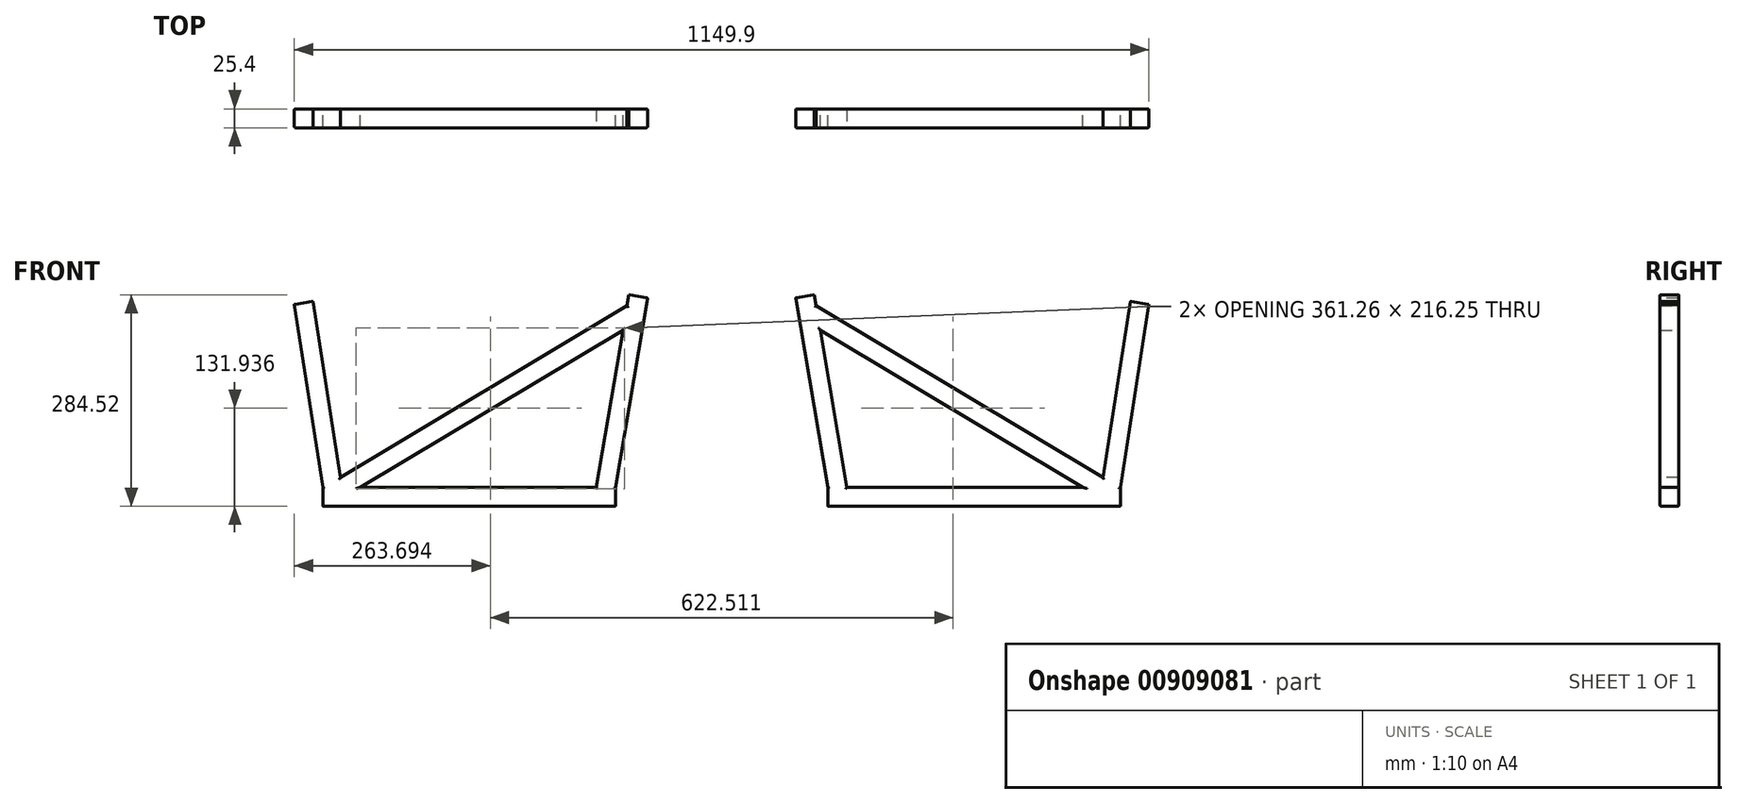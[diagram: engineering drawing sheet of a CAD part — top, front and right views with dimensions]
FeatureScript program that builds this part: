
annotation { "Feature Type Name" : "Feature", "Feature Type Description" : "" }
export const myFeature = defineFeature(function(context is Context, id is Id, definition is map)
    precondition{}
    {
        {
            var Q0;
            Q0=qCreatedBy(makeId("Front.planeOp"),FACE);
            var sketch = newSketch(context, id + "F0", { "sketchPlane" : qUnion([Q0])});
            skLineSegment(sketch, "E0", {"start": v(0, 0) * mm, "end": v(0, -387.35) * mm, "construction": true});
            skLineSegment(sketch, "E1", {"start": v(0, -387.35) * mm, "end": v(-552.45, -387.35) * mm, "construction": true});
            skLineSegment(sketch, "E2", {"start": v(-552.45, -387.35) * mm, "end": v(-574.68, -387.35) * mm, "construction": true});
            skCircle(sketch, "E3", {"center": v(-574.68, -387.35) * mm, "radius": 22.23 * mm});
            skLineSegment(sketch, "E4", {"start": v(0, -387.35) * mm, "end": v(0, -679.45) * mm, "construction": true});
            skLineSegment(sketch, "E5", {"start": v(0, -679.45) * mm, "end": v(-536.58, -679.45) * mm, "construction": true});
            skLineSegment(sketch, "E6", {"start": v(-536.58, -654.05) * mm, "end": v(-142.87, -654.05) * mm});
            skLineSegment(sketch, "E7", {"start": v(-574.68, -387.35) * mm, "end": v(-574.68, -409.58) * mm});
            skLineSegment(sketch, "E8", {"start": v(-574.68, -409.58) * mm, "end": v(0, -409.58) * mm, "construction": true});
            skLineSegment(sketch, "E9", {"start": v(0, -409.58) * mm, "end": v(-114.3, -409.58) * mm, "construction": true});
            skCircle(sketch, "E10", {"center": v(-114.3, -409.58) * mm, "radius": 12.7 * mm});
            skLineSegment(sketch, "E11", {"start": v(-536.58, -654.05) * mm, "end": v(-536.58, -679.45) * mm});
            skLineSegment(sketch, "E12", {"start": v(-536.58, -679.45) * mm, "end": v(-142.87, -679.45) * mm});
            skLineSegment(sketch, "E13", {"start": v(-142.87, -679.45) * mm, "end": v(-142.87, -654.05) * mm});
            skLineSegment(sketch, "E14", {"start": v(-536.58, -666.75) * mm, "end": v(-142.87, -666.75) * mm});
            skLineSegment(sketch, "E15", {"start": v(-574.68, -409.58) * mm, "end": v(-536.58, -654.05) * mm});
            skLineSegment(sketch, "E16", {"start": v(-555.63, -531.81) * mm, "end": v(-530.53, -527.9) * mm});
            skLineSegment(sketch, "E17", {"start": v(-530.53, -527.9) * mm, "end": v(-510.87, -654.05) * mm});
            skLineSegment(sketch, "E18", {"start": v(-530.53, -527.9) * mm, "end": v(-552.45, -387.23) * mm});
            skLineSegment(sketch, "E19", {"start": v(-142.87, -654.05) * mm, "end": v(-101.78, -411.7) * mm});
            skLineSegment(sketch, "E20", {"start": v(-101.78, -411.7) * mm, "end": v(-101.42, -409.58) * mm});
            skLineSegment(sketch, "E21", {"start": v(-122.33, -532.87) * mm, "end": v(-147.37, -528.63) * mm});
            skLineSegment(sketch, "E22", {"start": v(-147.37, -528.63) * mm, "end": v(-168.64, -654.05) * mm});
            skLineSegment(sketch, "E23", {"start": v(-147.37, -528.63) * mm, "end": v(-126.82, -407.45) * mm});
            skCircle(sketch, "E24", {"center": v(-510.87, -654.05) * mm, "radius": 12.7 * mm});
            skLineSegment(sketch, "E25", {"start": v(-127.18, -409.58) * mm, "end": v(-517.4, -643.15) * mm});
            skLineSegment(sketch, "E26", {"start": v(-322.29, -526.36) * mm, "end": v(-309.24, -548.16) * mm});
            skLineSegment(sketch, "E27", {"start": v(-309.24, -548.16) * mm, "end": v(-315.76, -537.26) * mm});
            skLineSegment(sketch, "E28", {"start": v(-309.24, -548.16) * mm, "end": v(-132.77, -442.52) * mm});
            skLineSegment(sketch, "E29", {"start": v(-309.24, -548.16) * mm, "end": v(-486.14, -654.05) * mm});
            skLineSegment(sketch, "E30", {"start": v(-339.72, -654.05) * mm, "end": v(-339.72, -679.45) * mm});
            skLineSegment(sketch, "E31", {"start": v(-315.76, -537.26) * mm, "end": v(-120.74, -420.52) * mm});
            skLineSegment(sketch, "E32", {"start": v(-315.76, -537.26) * mm, "end": v(-510.87, -654.05) * mm});
            skLineSegment(sketch, "E33", {"start": v(-543.08, -529.86) * mm, "end": v(-562.4, -405.88) * mm});
            skLineSegment(sketch, "E34", {"start": v(-543.08, -529.86) * mm, "end": v(-523.72, -654.05) * mm});
            skLineSegment(sketch, "E35", {"start": v(-134.85, -530.75) * mm, "end": v(-157.9, -666.75) * mm});
            skLineSegment(sketch, "E36", {"start": v(-523.72, -654.05) * mm, "end": v(-521.74, -666.75) * mm});
            skLineSegment(sketch, "E37", {"start": v(-134.85, -530.75) * mm, "end": v(-112.18, -397.05) * mm});
            skLineSegment(sketch, "E38", {"start": v(-510.87, -654.05) * mm, "end": v(-521.77, -660.57) * mm});
            skSolve(sketch);
        }
        {
            var Q0;
            Q0=sQuery(id+"F0.wireOp",EDGE,"E34");
            var Q1;
            Q1=sQuery(id+"F0.wireOp",VERTEX,"E33.start");
            cPlane(context, id + "F1", {"entities" : qUnion([Q0, Q1]), "cplaneType" : CPlaneType.LINE_POINT, "offset" : 25.4 * mm, "width" : 152.4 * mm, "height" : 152.4 * mm});
        }
        {
            var Q0;
            Q0=sQuery(id+"F0.wireOp",EDGE,"E26");
            cPoint(context, id + "F2", {"entities" : qUnion([Q0]), "parameter" : 0.5});
        }
        {
            var Q0;
            Q0=sQuery(id+"F0.wireOp",EDGE,"E32");
            var Q1;
            Q1 = qCreatedBy(id + "F2" ,VERTEX);
            cPlane(context, id + "F3", {"entities" : qUnion([Q0, Q1]), "cplaneType" : CPlaneType.LINE_POINT, "offset" : 25.4 * mm, "width" : 152.4 * mm, "height" : 152.4 * mm});
        }
        {
            var Q0;
            Q0=sQuery(id+"F0.wireOp",EDGE,"E35");
            var Q1;
            Q1=sQuery(id+"F0.wireOp",VERTEX,"E35.start");
            cPlane(context, id + "F4", {"entities" : qUnion([Q0, Q1]), "cplaneType" : CPlaneType.LINE_POINT, "offset" : 25.4 * mm, "width" : 152.4 * mm, "height" : 152.4 * mm});
        }
        {
            var Q0;
            Q0=sQuery(id+"F0.wireOp",EDGE,"E14");
            cPoint(context, id + "F5", {"entities" : qUnion([Q0]), "parameter" : 0.5});
        }
        {
            var Q0;
            Q0=sQuery(id+"F0.wireOp",EDGE,"E14");
            var Q1;
            Q1 = qCreatedBy(id + "F5" ,VERTEX);
            cPlane(context, id + "F6", {"entities" : qUnion([Q0, Q1]), "cplaneType" : CPlaneType.LINE_POINT, "offset" : 25.4 * mm, "width" : 152.4 * mm, "height" : 152.4 * mm});
        }
        {
            var Q0;
            Q0=qCreatedBy(id+"F1.planeOp",FACE);
            var sketch = newSketch(context, id + "F7", { "sketchPlane" : qUnion([Q0])});
            skLineSegment(sketch, "E39.bottom", {"start": v(-607.08, -12.7) * mm, "end": v(-629.3, -12.7) * mm});
            skLineSegment(sketch, "E39.top", {"start": v(-607.08, 12.7) * mm, "end": v(-629.3, 12.7) * mm});
            skLineSegment(sketch, "E39.left", {"start": v(-605.49, -11.11) * mm, "end": v(-605.49, 11.11) * mm});
            skLineSegment(sketch, "E39.right", {"start": v(-630.89, -11.11) * mm, "end": v(-630.89, 11.11) * mm});
            skPoint(sketch, "E39.middle", {"position": v(-618.19, 0) * mm});
            skPoint(sketch, "E40.visualSharp", {"position": v(-630.89, 12.7) * mm});
            skArc(sketch, "E40.filletArc", {"start": v(-629.3, 12.7) * mm, "mid": v(-630.42, 12.24) * mm, "end": v(-630.89, 11.11) * mm});
            skPoint(sketch, "E41.visualSharp", {"position": v(-605.49, 12.7) * mm});
            skArc(sketch, "E41.filletArc", {"start": v(-605.49, 11.11) * mm, "mid": v(-605.95, 12.24) * mm, "end": v(-607.08, 12.7) * mm});
            skPoint(sketch, "E42.visualSharp", {"position": v(-605.49, -12.7) * mm});
            skArc(sketch, "E42.filletArc", {"start": v(-607.08, -12.7) * mm, "mid": v(-605.95, -12.24) * mm, "end": v(-605.49, -11.11) * mm});
            skPoint(sketch, "E43.visualSharp", {"position": v(-630.89, -12.7) * mm});
            skArc(sketch, "E43.filletArc", {"start": v(-630.89, -11.11) * mm, "mid": v(-630.42, -12.24) * mm, "end": v(-629.3, -12.7) * mm});
            skSolve(sketch);
        }
        {
            var Q0;
            Q0=qCreatedBy(id+"F4.planeOp",FACE);
            var sketch = newSketch(context, id + "F8", { "sketchPlane" : qUnion([Q0])});
            skLineSegment(sketch, "E44.bottom", {"start": v(-33.1, -12.7) * mm, "end": v(-55.33, -12.7) * mm});
            skLineSegment(sketch, "E44.top", {"start": v(-33.1, 12.7) * mm, "end": v(-55.33, 12.7) * mm});
            skLineSegment(sketch, "E44.left", {"start": v(-31.52, -11.11) * mm, "end": v(-31.52, 11.11) * mm});
            skLineSegment(sketch, "E44.right", {"start": v(-56.92, -11.11) * mm, "end": v(-56.92, 11.11) * mm});
            skPoint(sketch, "E44.middle", {"position": v(-44.22, 0) * mm});
            skPoint(sketch, "E45.visualSharp", {"position": v(-56.92, 12.7) * mm});
            skArc(sketch, "E45.filletArc", {"start": v(-55.33, 12.7) * mm, "mid": v(-56.45, 12.24) * mm, "end": v(-56.92, 11.11) * mm});
            skPoint(sketch, "E46.visualSharp", {"position": v(-31.52, 12.7) * mm});
            skArc(sketch, "E46.filletArc", {"start": v(-31.52, 11.11) * mm, "mid": v(-31.98, 12.24) * mm, "end": v(-33.1, 12.7) * mm});
            skPoint(sketch, "E47.visualSharp", {"position": v(-31.52, -12.7) * mm});
            skArc(sketch, "E47.filletArc", {"start": v(-33.1, -12.7) * mm, "mid": v(-31.98, -12.24) * mm, "end": v(-31.52, -11.11) * mm});
            skPoint(sketch, "E48.visualSharp", {"position": v(-56.92, -12.7) * mm});
            skArc(sketch, "E48.filletArc", {"start": v(-56.92, -11.11) * mm, "mid": v(-56.45, -12.24) * mm, "end": v(-55.33, -12.7) * mm});
            skSolve(sketch);
        }
        {
            var Q0;
            Q0=qCreatedBy(id+"F3.planeOp",FACE);
            var sketch = newSketch(context, id + "F9", { "sketchPlane" : qUnion([Q0])});
            skLineSegment(sketch, "E49.bottom", {"start": v(-11.11, -311.5) * mm, "end": v(11.11, -311.5) * mm});
            skLineSegment(sketch, "E49.top", {"start": v(-11.11, -286.1) * mm, "end": v(11.11, -286.1) * mm});
            skLineSegment(sketch, "E49.left", {"start": v(-12.7, -309.92) * mm, "end": v(-12.7, -287.7) * mm});
            skLineSegment(sketch, "E49.right", {"start": v(12.7, -309.92) * mm, "end": v(12.7, -287.7) * mm});
            skPoint(sketch, "E49.middle", {"position": v(0, -298.8) * mm});
            skPoint(sketch, "E50.visualSharp", {"position": v(12.7, -286.1) * mm});
            skArc(sketch, "E50.filletArc", {"start": v(12.7, -287.7) * mm, "mid": v(12.24, -286.57) * mm, "end": v(11.11, -286.1) * mm});
            skPoint(sketch, "E51.visualSharp", {"position": v(12.7, -311.5) * mm});
            skArc(sketch, "E51.filletArc", {"start": v(11.11, -311.5) * mm, "mid": v(12.24, -311.04) * mm, "end": v(12.7, -309.92) * mm});
            skPoint(sketch, "E52.visualSharp", {"position": v(-12.7, -311.5) * mm});
            skArc(sketch, "E52.filletArc", {"start": v(-12.7, -309.92) * mm, "mid": v(-12.24, -311.04) * mm, "end": v(-11.11, -311.5) * mm});
            skPoint(sketch, "E53.visualSharp", {"position": v(-12.7, -286.1) * mm});
            skArc(sketch, "E53.filletArc", {"start": v(-11.11, -286.1) * mm, "mid": v(-12.24, -286.57) * mm, "end": v(-12.7, -287.7) * mm});
            skSolve(sketch);
        }
        {
            var Q0;
            Q0=qCreatedBy(id+"F6.planeOp",FACE);
            var sketch = newSketch(context, id + "F10", { "sketchPlane" : qUnion([Q0])});
            skLineSegment(sketch, "E54.bottom", {"start": v(-11.11, -679.45) * mm, "end": v(11.11, -679.45) * mm});
            skLineSegment(sketch, "E54.top", {"start": v(-11.11, -654.05) * mm, "end": v(11.11, -654.05) * mm});
            skLineSegment(sketch, "E54.left", {"start": v(-12.7, -677.86) * mm, "end": v(-12.7, -655.64) * mm});
            skLineSegment(sketch, "E54.right", {"start": v(12.7, -677.86) * mm, "end": v(12.7, -655.64) * mm});
            skPoint(sketch, "E54.middle", {"position": v(0, -666.75) * mm});
            skPoint(sketch, "E55.visualSharp", {"position": v(-12.7, -654.05) * mm});
            skArc(sketch, "E55.filletArc", {"start": v(-11.11, -654.05) * mm, "mid": v(-12.24, -654.51) * mm, "end": v(-12.7, -655.64) * mm});
            skPoint(sketch, "E56.visualSharp", {"position": v(-12.7, -679.45) * mm});
            skArc(sketch, "E56.filletArc", {"start": v(-12.7, -677.86) * mm, "mid": v(-12.24, -678.99) * mm, "end": v(-11.11, -679.45) * mm});
            skPoint(sketch, "E57.visualSharp", {"position": v(12.7, -679.45) * mm});
            skArc(sketch, "E57.filletArc", {"start": v(11.11, -679.45) * mm, "mid": v(12.24, -678.99) * mm, "end": v(12.7, -677.86) * mm});
            skPoint(sketch, "E58.visualSharp", {"position": v(12.7, -654.05) * mm});
            skArc(sketch, "E58.filletArc", {"start": v(12.7, -655.64) * mm, "mid": v(12.24, -654.51) * mm, "end": v(11.11, -654.05) * mm});
            skSolve(sketch);
        }
        {
            var Q0;
            Q0=makeQuery(id+"F7.imprint","IMPRINT",FACE,{"disambiguationData":[TD([[makeQuery(id+"F7.imprint","IMPRINT",EDGE,{"derivedFrom":sQuery(id+"F7.wireOp",EDGE,"E39.bottom")}),-1.0]])]});
            var Q1;
            Q1=sQuery(id+"F0.wireOp",EDGE,"E33");
            var Q2;
            Q2=sQuery(id+"F0.wireOp",EDGE,"E34");
            var Q3;
            Q3=sQuery(id+"F0.wireOp",EDGE,"E36");
            sweep(context, id + "F11", {"profiles" : qUnion([Q0]), "path" : qUnion([Q1, Q2, Q3])});
        }
        {
            var Q0;
            Q0=makeQuery(id+"F10.imprint","IMPRINT",FACE,{"disambiguationData":[TD([[makeQuery(id+"F10.imprint","IMPRINT",EDGE,{"derivedFrom":sQuery(id+"F10.wireOp",EDGE,"E54.bottom")}),1.0]])]});
            var Q1;
            Q1=sQuery(id+"F0.wireOp",EDGE,"E14");
            sweep(context, id + "F12", {"operationType" : NewBodyOperationType.ADD, "profiles" : qUnion([Q0]), "path" : qUnion([Q1])});
        }
        {
            var Q0;
            Q0=makeQuery(id+"F9.imprint","IMPRINT",FACE,{"disambiguationData":[TD([[makeQuery(id+"F9.imprint","IMPRINT",EDGE,{"derivedFrom":sQuery(id+"F9.wireOp",EDGE,"E49.bottom")}),1.0]])]});
            var Q1;
            Q1=sQuery(id+"F0.wireOp",EDGE,"E32");
            var Q2;
            Q2=sQuery(id+"F0.wireOp",EDGE,"E38");
            var Q3;
            Q3=sQuery(id+"F0.wireOp",EDGE,"E31");
            sweep(context, id + "F13", {"operationType" : NewBodyOperationType.ADD, "profiles" : qUnion([Q0]), "path" : qUnion([Q1, Q2, Q3])});
        }
        {
            var Q0;
            Q0=makeQuery(id+"F8.imprint","IMPRINT",FACE,{"disambiguationData":[TD([[makeQuery(id+"F8.imprint","IMPRINT",EDGE,{"derivedFrom":sQuery(id+"F8.wireOp",EDGE,"E44.bottom")}),-1.0]])]});
            var Q1;
            Q1=sQuery(id+"F0.wireOp",EDGE,"E35");
            var Q2;
            Q2=sQuery(id+"F0.wireOp",EDGE,"E37");
            sweep(context, id + "F14", {"operationType" : NewBodyOperationType.ADD, "profiles" : qUnion([Q0]), "path" : qUnion([Q1, Q2])});
        }
        {
            var Q0;
            Q0=makeQuery(id+"F11.opSweep","SWEPT_BODY",BODY,{"disambiguationData":[OSD([sQuery(id+"F0.wireOp",EDGE,"E36"),sQuery(id+"F7.wireOp",EDGE,"E39.bottom"),sQuery(id+"F7.wireOp",EDGE,"E39.top"),sQuery(id+"F7.wireOp",EDGE,"E39.left"),sQuery(id+"F7.wireOp",EDGE,"E39.right"),sQuery(id+"F7.wireOp",EDGE,"E40.filletArc"),sQuery(id+"F7.wireOp",EDGE,"E41.filletArc"),sQuery(id+"F7.wireOp",EDGE,"E42.filletArc"),sQuery(id+"F7.wireOp",EDGE,"E43.filletArc")])]});
            var Q1;
            Q1=qCreatedBy(makeId("Right.planeOp"),FACE);
            mirror(context, id + "F15", {"entities" : qUnion([Q0]), "mirrorPlane" : qUnion([Q1])});
        }
    });
